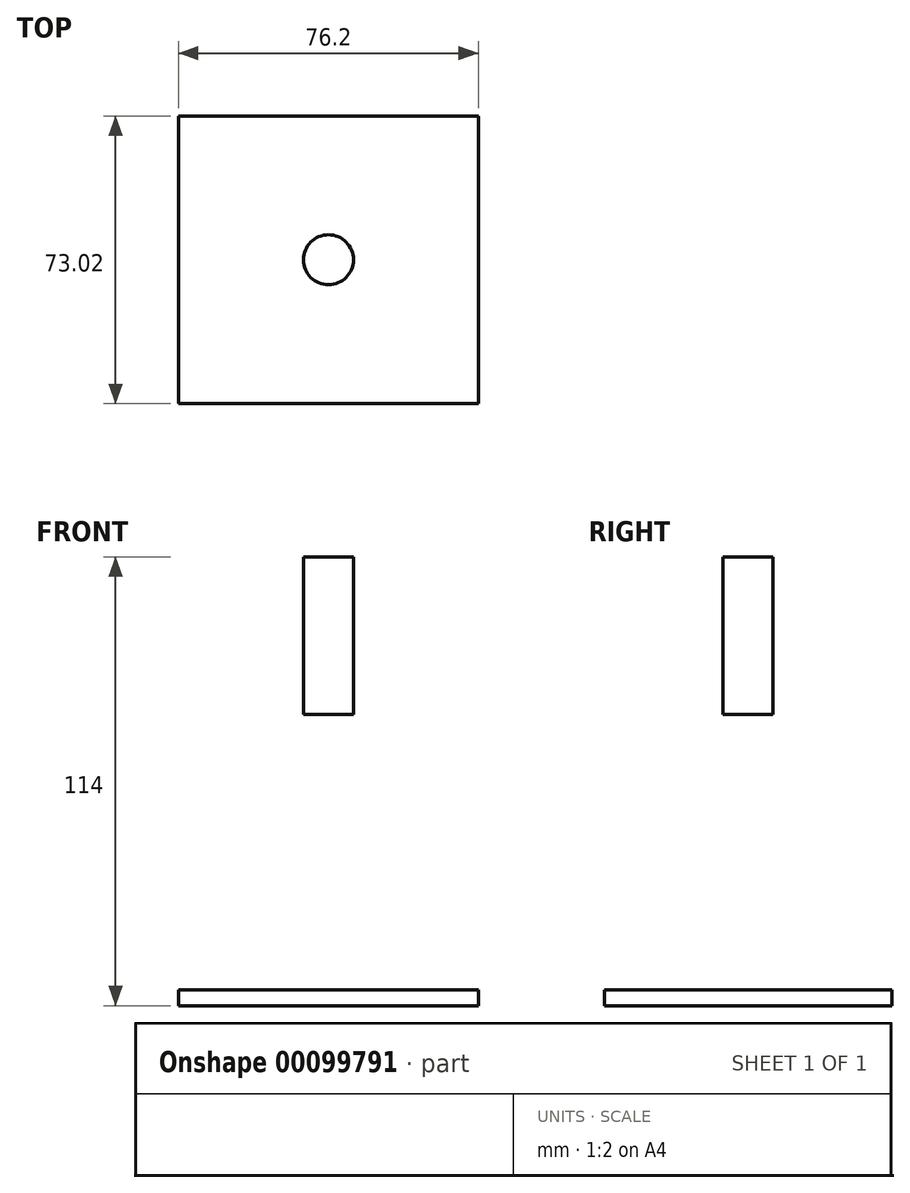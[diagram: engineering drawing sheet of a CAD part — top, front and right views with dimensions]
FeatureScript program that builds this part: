
annotation { "Feature Type Name" : "Feature", "Feature Type Description" : "" }
export const myFeature = defineFeature(function(context is Context, id is Id, definition is map)
    precondition{}
    {
        {
            var Q0;
            Q0=qCreatedBy(makeId("Top.planeOp"),FACE);
            var sketch = newSketch(context, id + "F0", { "sketchPlane" : qUnion([Q0])});
            skLineSegment(sketch, "E0.bottom", {"start": v(38.1, -36.51) * mm, "end": v(-38.1, -36.51) * mm});
            skLineSegment(sketch, "E0.top", {"start": v(38.1, 36.51) * mm, "end": v(-38.1, 36.51) * mm});
            skLineSegment(sketch, "E0.left", {"start": v(38.1, -36.51) * mm, "end": v(38.1, 36.51) * mm});
            skLineSegment(sketch, "E0.right", {"start": v(-38.1, -36.51) * mm, "end": v(-38.1, 36.51) * mm});
            skPoint(sketch, "E0.middle", {"position": v(0, 0) * mm});
            skSolve(sketch);
        }
        {
            var Q0;
            Q0=makeQuery(id+"F0.imprint","IMPRINT",FACE,{"disambiguationData":[TD([[makeQuery(id+"F0.imprint","IMPRINT",EDGE,{"derivedFrom":sQuery(id+"F0.wireOp",EDGE,"E0.bottom")}),-1.0]])]});
            extrude(context, id + "F1", {"entities" : qUnion([Q0]), "depth" : 4 * mm});
        }
        {
            var Q0;
            Q0=makeQuery(id+"F1.opExtrude","CAP_FACE",FACE,{"disambiguationData":[OSD([sQuery(id+"F0.wireOp",EDGE,"E0.bottom"),sQuery(id+"F0.wireOp",EDGE,"E0.top"),sQuery(id+"F0.wireOp",EDGE,"E0.left"),sQuery(id+"F0.wireOp",EDGE,"E0.right")])],"isStart":false});
            cPlane(context, id + "F2", {"entities" : qUnion([Q0]), "cplaneType" : CPlaneType.OFFSET, "offset" : 70 * mm, "width" : 150 * mm, "height" : 150 * mm});
        }
        {
            var Q0;
            Q0=qCreatedBy(id+"F2.planeOp",FACE);
            var sketch = newSketch(context, id + "F3", { "sketchPlane" : qUnion([Q0])});
            skCircle(sketch, "E1", {"center": v(0, 0) * mm, "radius": 6.35 * mm});
            skSolve(sketch);
        }
        {
            var Q0;
            Q0=makeQuery(id+"F3.imprint","IMPRINT",FACE,{"disambiguationData":[TD([[makeQuery(id+"F3.imprint","IMPRINT",EDGE,{"derivedFrom":sQuery(id+"F3.wireOp",EDGE,"E1")}),1.0]])]});
            extrude(context, id + "F4", {"entities" : qUnion([Q0]), "depth" : 40 * mm});
        }
    });
